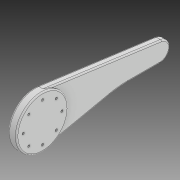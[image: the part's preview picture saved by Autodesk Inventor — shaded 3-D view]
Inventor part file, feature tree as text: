
AUTODESK INVENTOR PART (.ipt)
format: ipt  version: 2020 (Build 240168000, 168)  size: 172,032 bytes
history: native  units: mm
features: extrude x2, sketch x2, fillet x1, projected_geometry x1
ambient origin geometry x8: Origin, YZ Plane, XZ Plane, XY Plane, X Axis, Y Axis, Z Axis, Center Point
bodies: Solid1 (feature_tree)
feature tree (6):
  extrude  "Extrusion1"  Depth=80.0mm
  extrude  "Extrusion2"  Depth=2.0mm
  fillet  "Fillet1"  Radius=130.0mm
  sketch  "Sketch1"  dims[d0=60.0mm d1=80.0mm]
  sketch  "Sketch2"  dims[d2=30.0mm d3=240.0mm d4=130.0mm d5=50.0mm d6=3.5mm d7=80.0mm d9=360.0deg d11=10.0mm d12=0.0mm d13=3.0mm d14=0.0mm d15=185.0mm d16=2.0mm]
  projected_geometry  "Projected Loop1"
